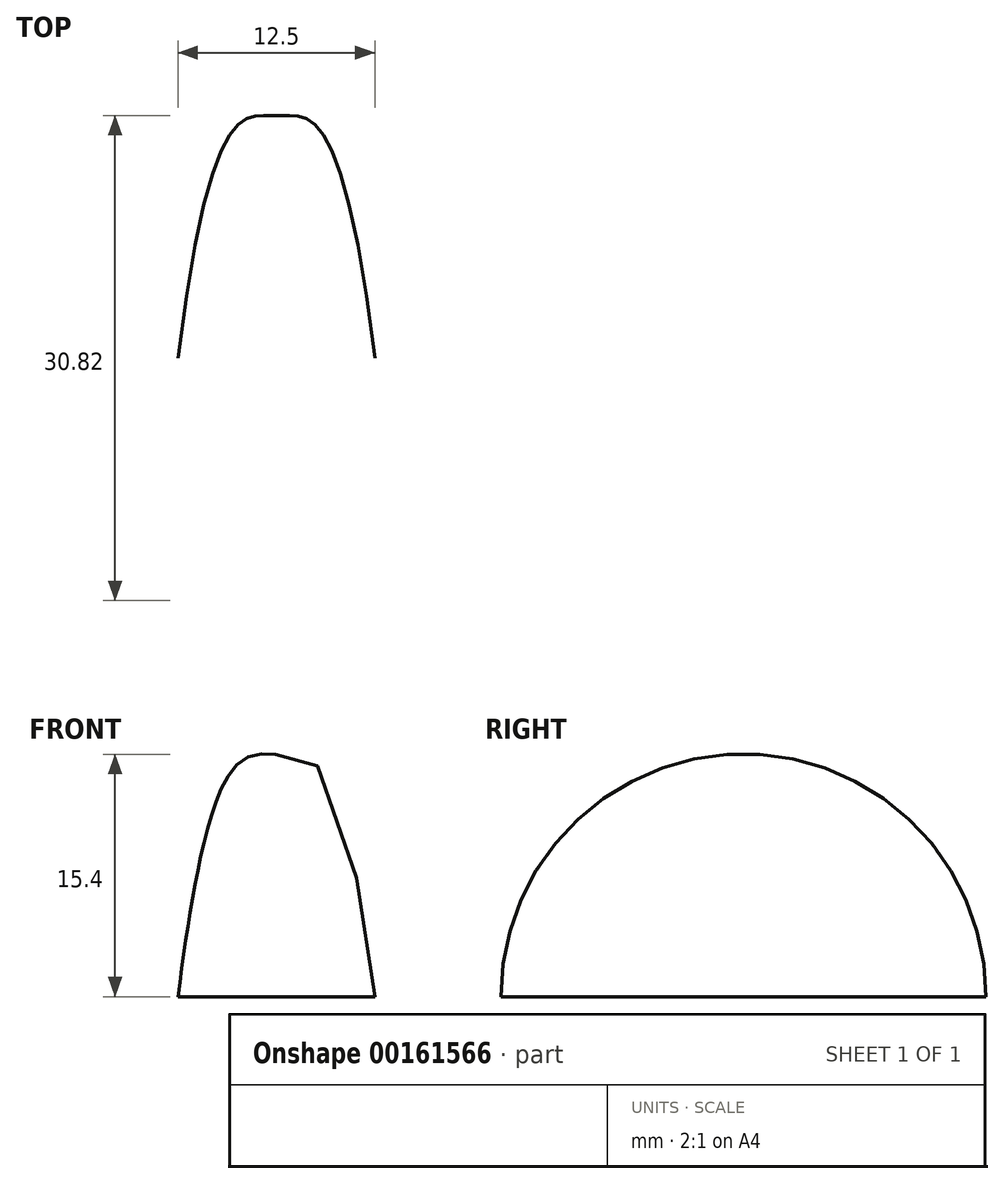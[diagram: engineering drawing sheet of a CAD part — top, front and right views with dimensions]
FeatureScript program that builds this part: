
annotation { "Feature Type Name" : "Feature", "Feature Type Description" : "" }
export const myFeature = defineFeature(function(context is Context, id is Id, definition is map)
    precondition{}
    {
        {
            var Q0;
            Q0=qCreatedBy(makeId("Top.planeOp"),FACE);
            var sketch = newSketch(context, id + "F0", { "sketchPlane" : qUnion([Q0])});
            skPoint(sketch, "E0", {"position": v(-6.25, 0) * mm});
            skPoint(sketch, "E1", {"position": v(0, 15.38) * mm});
            skPoint(sketch, "E2", {"position": v(6.25, 0) * mm});
            skFitSpline(sketch, "E3", {"points": [v(-6.25, 0) * mm, v(0, 15.38) * mm, v(6.25, 0) * mm], "startDerivative": vector(12.5, 100) * mm, "endDerivative": vector(12.5, -100) * mm});
            skLineSegment(sketch, "E4", {"start": v(-6.25, 0) * mm, "end": v(6.25, 0) * mm});
            skSolve(sketch);
        }
        {
            var Q0;
            Q0 = qSketchRegion(id + "F0", true);
            var Q1;
            Q1=sQuery(id+"F0.wireOp",EDGE,"E4");
            revolve(context, id + "F1", {"entities" : qUnion([Q0]), "axis" : qUnion([Q1]), "revolveType" : RevolveType.ONE_DIRECTION, "angle" : 180 * degree});
        }
    });
